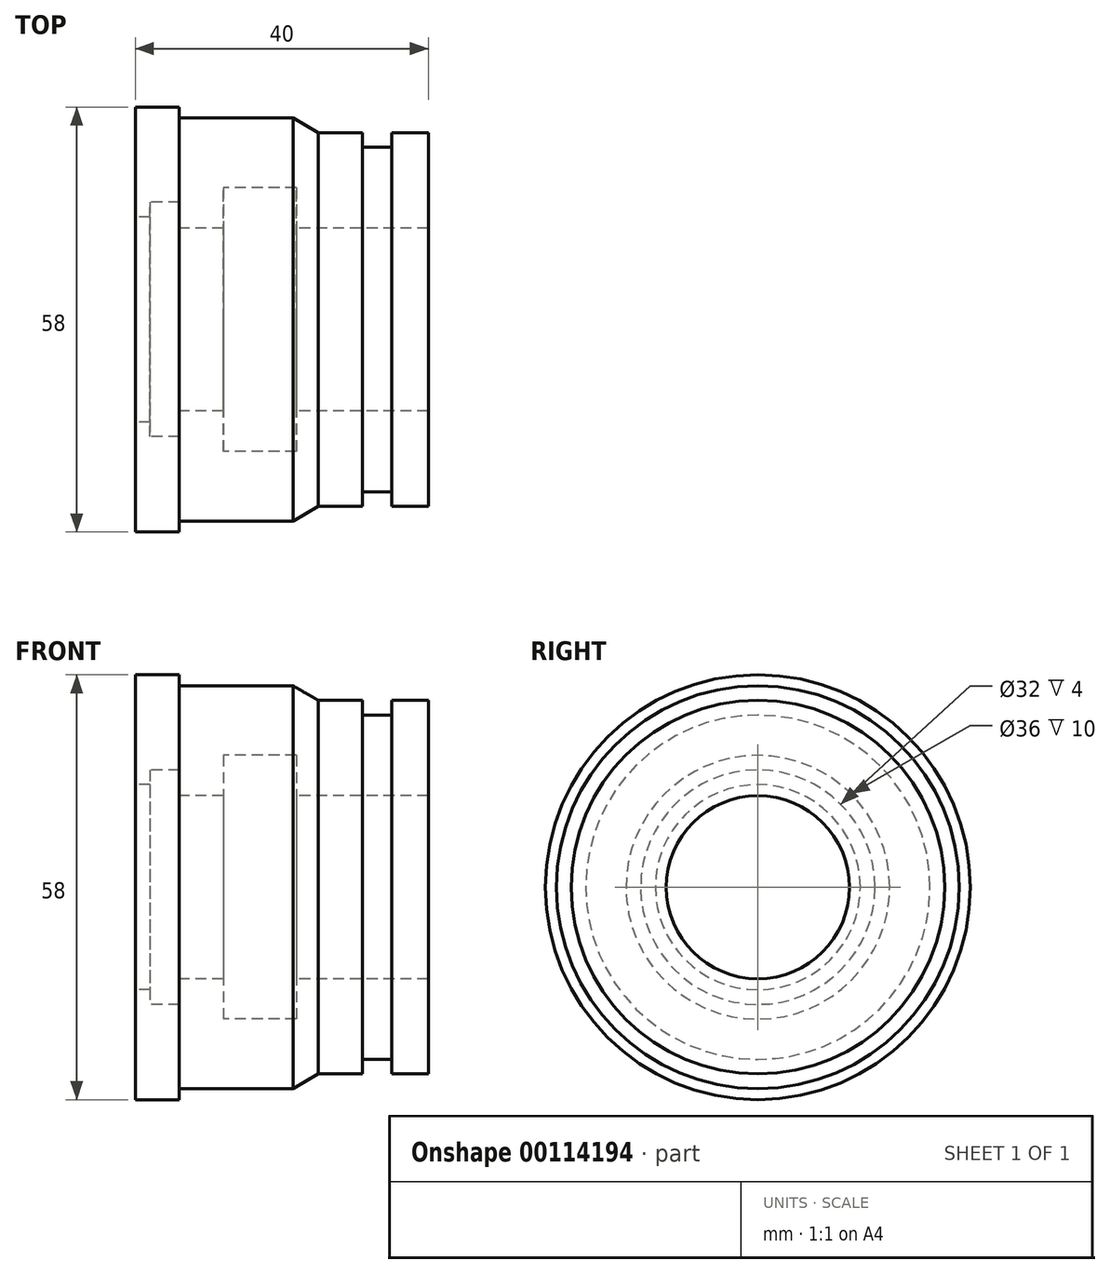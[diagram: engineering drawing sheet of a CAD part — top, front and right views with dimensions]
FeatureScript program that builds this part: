
annotation { "Feature Type Name" : "Feature", "Feature Type Description" : "" }
export const myFeature = defineFeature(function(context is Context, id is Id, definition is map)
    precondition{}
    {
        {
            var Q0;
            Q0=qCreatedBy(makeId("Front.planeOp"),FACE);
            var sketch = newSketch(context, id + "F0", { "sketchPlane" : qUnion([Q0])});
            skLineSegment(sketch, "E0", {"start": v(0, 0) * mm, "end": v(250.98, 0) * mm});
            skCircle(sketch, "E1", {"center": v(0, 0) * mm, "radius": 15 * mm});
            skCircle(sketch, "E2", {"center": v(0, 0) * mm, "radius": 27.5 * mm});
            skLineSegment(sketch, "E3", {"start": v(24.5, 12.5) * mm, "end": v(205, 12.5) * mm});
            skLineSegment(sketch, "E4", {"start": v(250, 8) * mm, "end": v(250, 0) * mm});
            skLineSegment(sketch, "E5", {"start": v(205, 12.5) * mm, "end": v(205, 8.5) * mm});
            skLineSegment(sketch, "E6", {"start": v(205, 8.5) * mm, "end": v(225, 8.5) * mm});
            skLineSegment(sketch, "E7", {"start": v(225, 8.5) * mm, "end": v(225, 8) * mm});
            skLineSegment(sketch, "E8", {"start": v(225, 8) * mm, "end": v(250, 8) * mm});
            skSolve(sketch);
        }
        {
            var Q0;
            Q0=qCreatedBy(makeId("Front.planeOp"),FACE);
            var sketch = newSketch(context, id + "F1", { "sketchPlane" : qUnion([Q0])});
            skLineSegment(sketch, "E9", {"start": v(54.7, 12.5) * mm, "end": v(54.7, 29) * mm});
            skLineSegment(sketch, "E10", {"start": v(54.7, 29) * mm, "end": v(60.7, 29) * mm});
            skLineSegment(sketch, "E11", {"start": v(60.7, 29) * mm, "end": v(60.7, 27.5) * mm});
            skLineSegment(sketch, "E12", {"start": v(60.7, 27.5) * mm, "end": v(76.24, 27.5) * mm});
            skLineSegment(sketch, "E13", {"start": v(76.24, 27.5) * mm, "end": v(79.7, 25.5) * mm});
            skLineSegment(sketch, "E14", {"start": v(79.7, 25.5) * mm, "end": v(94.7, 25.5) * mm});
            skLineSegment(sketch, "E15", {"start": v(94.7, 25.5) * mm, "end": v(94.7, 12.5) * mm});
            skLineSegment(sketch, "E16", {"start": v(94.7, 12.5) * mm, "end": v(54.7, 12.5) * mm});
            skLineSegment(sketch, "E17", {"start": v(66.7, 12.5) * mm, "end": v(66.7, 18) * mm});
            skLineSegment(sketch, "E18", {"start": v(66.7, 18) * mm, "end": v(76.7, 18) * mm});
            skLineSegment(sketch, "E19", {"start": v(76.7, 18) * mm, "end": v(76.7, 12.5) * mm});
            skLineSegment(sketch, "E20", {"start": v(54.7, 14) * mm, "end": v(56.7, 14) * mm});
            skLineSegment(sketch, "E21", {"start": v(56.7, 14) * mm, "end": v(56.7, 16) * mm});
            skLineSegment(sketch, "E22", {"start": v(56.7, 16) * mm, "end": v(60.7, 16) * mm});
            skLineSegment(sketch, "E23", {"start": v(60.7, 16) * mm, "end": v(60.7, 12.5) * mm});
            skLineSegment(sketch, "E24.bottom", {"start": v(85.7, 25.5) * mm, "end": v(89.7, 25.5) * mm});
            skLineSegment(sketch, "E24.top", {"start": v(85.7, 23.5) * mm, "end": v(89.7, 23.5) * mm});
            skLineSegment(sketch, "E24.left", {"start": v(85.7, 25.5) * mm, "end": v(85.7, 23.5) * mm});
            skLineSegment(sketch, "E24.right", {"start": v(89.7, 25.5) * mm, "end": v(89.7, 23.5) * mm});
            skLineSegment(sketch, "E25", {"start": v(48.25, 0) * mm, "end": v(103.65, 0) * mm});
            skSolve(sketch);
        }
        {
            var Q0;
            {var subQ10=sQuery(id+"F1.wireOp",EDGE,"E10");Q0=makeQuery(id+"F1.imprint","IMPRINT",FACE,{"disambiguationData":[TD([[makeQuery(id+"F1.imprint","IMPRINT",EDGE,{"derivedFrom":subQ10}),-1.0]])]});}
            var Q1;
            Q1=sQuery(id+"F1.wireOp",EDGE,"E25");
            revolve(context, id + "F2", {"entities" : qUnion([Q0]), "axis" : qUnion([Q1]), "revolveType" : RevolveType.FULL});
        }
    });
